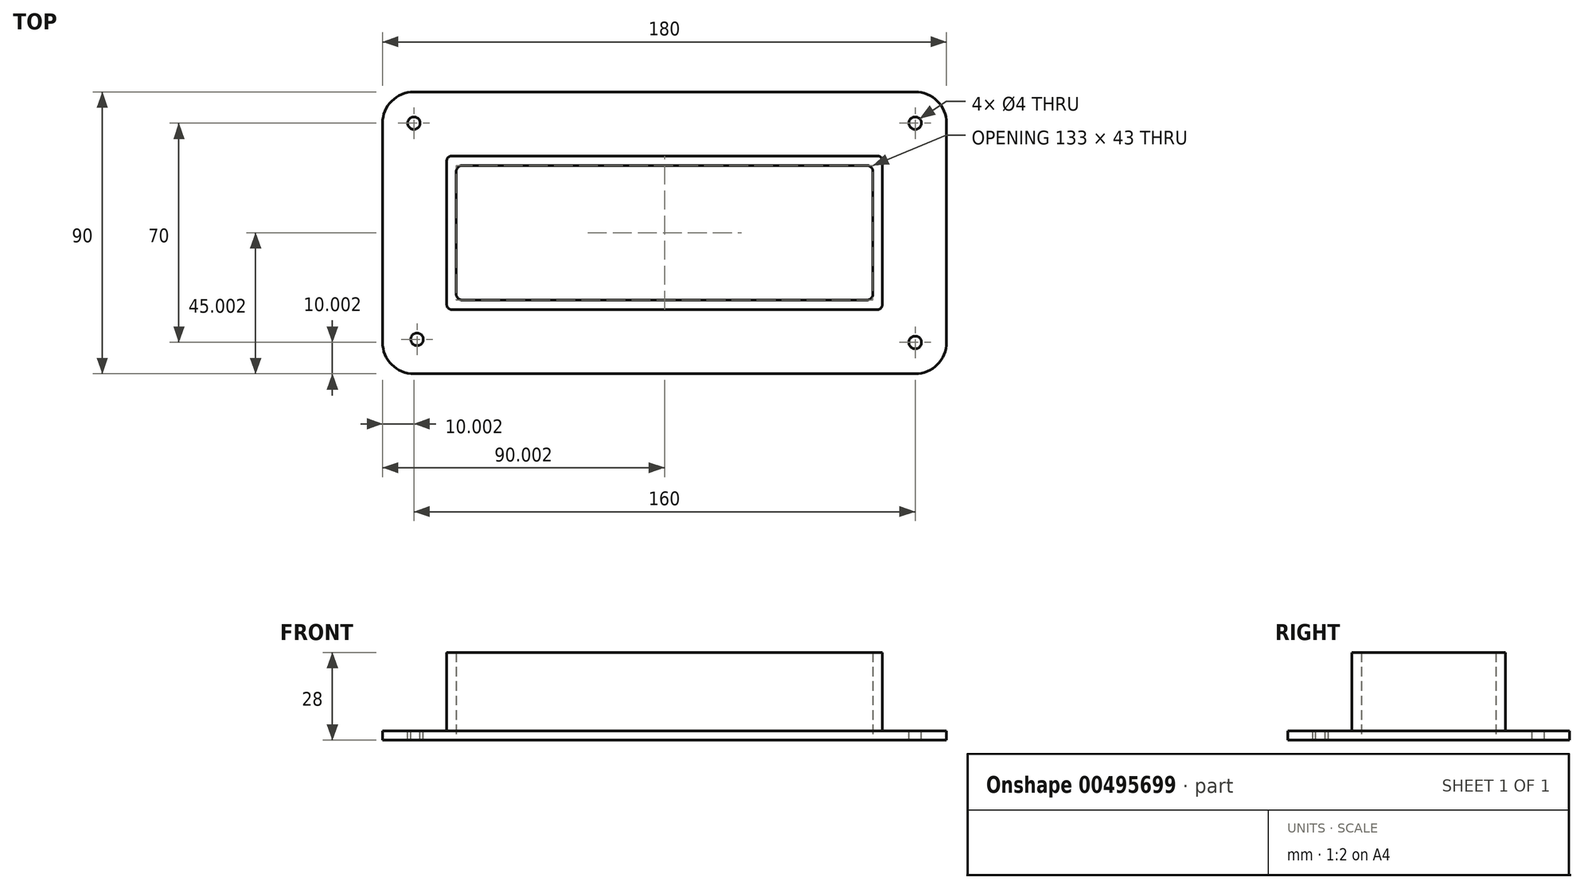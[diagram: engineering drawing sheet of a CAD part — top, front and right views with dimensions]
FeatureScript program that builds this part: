
annotation { "Feature Type Name" : "Feature", "Feature Type Description" : "" }
export const myFeature = defineFeature(function(context is Context, id is Id, definition is map)
    precondition{}
    {
        {
            var Q0;
            Q0=qCreatedBy(makeId("Top.planeOp"),FACE);
            var sketch = newSketch(context, id + "F0", { "sketchPlane" : qUnion([Q0])});
            skLineSegment(sketch, "E0.bottom", {"start": v(-68.03, 24.97) * mm, "end": v(67.97, 24.97) * mm});
            skLineSegment(sketch, "E0.top", {"start": v(-68.03, -25.03) * mm, "end": v(67.97, -25.03) * mm});
            skLineSegment(sketch, "E0.left", {"start": v(-70.03, 22.97) * mm, "end": v(-70.03, -23.03) * mm});
            skLineSegment(sketch, "E0.right", {"start": v(69.97, 22.97) * mm, "end": v(69.97, -23.03) * mm});
            skLineSegment(sketch, "E1.0", {"start": v(-90.03, 34.97) * mm, "end": v(-90.03, -35.03) * mm});
            skLineSegment(sketch, "E1.1", {"start": v(-80.03, 44.97) * mm, "end": v(79.97, 44.97) * mm});
            skLineSegment(sketch, "E1.2", {"start": v(89.97, 34.97) * mm, "end": v(89.97, -35.03) * mm});
            skLineSegment(sketch, "E1.3", {"start": v(-80.03, -45.03) * mm, "end": v(79.97, -45.03) * mm});
            skPoint(sketch, "E2.visualSharp", {"position": v(-90.03, -45.03) * mm});
            skArc(sketch, "E2.filletArc", {"start": v(-90.03, -35.03) * mm, "mid": v(-87.1, -42.1) * mm, "end": v(-80.03, -45.03) * mm});
            skPoint(sketch, "E3.visualSharp", {"position": v(-90.03, 44.97) * mm});
            skArc(sketch, "E3.filletArc", {"start": v(-80.03, 44.97) * mm, "mid": v(-87.1, 42.04) * mm, "end": v(-90.03, 34.97) * mm});
            skPoint(sketch, "E4.visualSharp", {"position": v(89.97, 44.97) * mm});
            skArc(sketch, "E4.filletArc", {"start": v(89.97, 34.97) * mm, "mid": v(87.04, 42.04) * mm, "end": v(79.97, 44.97) * mm});
            skPoint(sketch, "E5.visualSharp", {"position": v(89.97, -45.03) * mm});
            skArc(sketch, "E5.filletArc", {"start": v(79.97, -45.03) * mm, "mid": v(87.04, -42.1) * mm, "end": v(89.97, -35.03) * mm});
            skPoint(sketch, "E6.visualSharp", {"position": v(-70.03, 24.97) * mm});
            skArc(sketch, "E6.filletArc", {"start": v(-68.03, 24.97) * mm, "mid": v(-69.44, 24.39) * mm, "end": v(-70.03, 22.97) * mm});
            skPoint(sketch, "E7.visualSharp", {"position": v(-70.03, -25.03) * mm});
            skArc(sketch, "E7.filletArc", {"start": v(-70.03, -23.03) * mm, "mid": v(-69.44, -24.44) * mm, "end": v(-68.03, -25.03) * mm});
            skPoint(sketch, "E8.visualSharp", {"position": v(69.97, -25.03) * mm});
            skArc(sketch, "E8.filletArc", {"start": v(67.97, -25.03) * mm, "mid": v(69.39, -24.44) * mm, "end": v(69.97, -23.03) * mm});
            skPoint(sketch, "E9.visualSharp", {"position": v(69.97, 24.97) * mm});
            skArc(sketch, "E9.filletArc", {"start": v(69.97, 22.97) * mm, "mid": v(69.39, 24.39) * mm, "end": v(67.97, 24.97) * mm});
            skCircle(sketch, "E10", {"center": v(-80.03, 34.97) * mm, "radius": 2 * mm});
            skCircle(sketch, "E11", {"center": v(-79.03, -34.03) * mm, "radius": 2 * mm});
            skCircle(sketch, "E12", {"center": v(79.97, -35.03) * mm, "radius": 2 * mm});
            skCircle(sketch, "E13", {"center": v(79.97, 34.97) * mm, "radius": 2 * mm});
            skArc(sketch, "E14.0", {"start": v(-68.03, 24.47) * mm, "mid": v(-69.09, 24.03) * mm, "end": v(-69.53, 22.97) * mm});
            skLineSegment(sketch, "E14.1", {"start": v(-68.03, 24.47) * mm, "end": v(67.97, 24.47) * mm});
            skLineSegment(sketch, "E14.2", {"start": v(-69.53, 22.97) * mm, "end": v(-69.53, -23.03) * mm});
            skArc(sketch, "E14.3", {"start": v(69.47, 22.97) * mm, "mid": v(69.03, 24.03) * mm, "end": v(67.97, 24.47) * mm});
            skArc(sketch, "E14.4", {"start": v(-69.53, -23.03) * mm, "mid": v(-69.09, -24.09) * mm, "end": v(-68.03, -24.53) * mm});
            skLineSegment(sketch, "E14.5", {"start": v(-68.03, -24.53) * mm, "end": v(67.97, -24.53) * mm});
            skArc(sketch, "E14.6", {"start": v(67.97, -24.53) * mm, "mid": v(69.03, -24.09) * mm, "end": v(69.47, -23.03) * mm});
            skLineSegment(sketch, "E14.7", {"start": v(69.47, 22.97) * mm, "end": v(69.47, -23.03) * mm});
            skLineSegment(sketch, "E15.0", {"start": v(-66.53, 19.47) * mm, "end": v(-66.53, -19.53) * mm});
            skLineSegment(sketch, "E15.1", {"start": v(-64.53, 21.47) * mm, "end": v(64.47, 21.47) * mm});
            skLineSegment(sketch, "E15.2", {"start": v(66.47, 19.47) * mm, "end": v(66.47, -19.53) * mm});
            skLineSegment(sketch, "E15.3", {"start": v(-64.53, -21.53) * mm, "end": v(64.47, -21.53) * mm});
            skPoint(sketch, "E16.visualSharp", {"position": v(-66.53, 21.47) * mm});
            skArc(sketch, "E16.filletArc", {"start": v(-64.53, 21.47) * mm, "mid": v(-65.94, 20.89) * mm, "end": v(-66.53, 19.47) * mm});
            skPoint(sketch, "E17.visualSharp", {"position": v(-66.53, -21.53) * mm});
            skArc(sketch, "E17.filletArc", {"start": v(-66.53, -19.53) * mm, "mid": v(-65.94, -20.94) * mm, "end": v(-64.53, -21.53) * mm});
            skPoint(sketch, "E18.visualSharp", {"position": v(66.47, -21.53) * mm});
            skArc(sketch, "E18.filletArc", {"start": v(64.47, -21.53) * mm, "mid": v(65.89, -20.94) * mm, "end": v(66.47, -19.53) * mm});
            skPoint(sketch, "E19.visualSharp", {"position": v(66.47, 21.47) * mm});
            skArc(sketch, "E19.filletArc", {"start": v(66.47, 19.47) * mm, "mid": v(65.89, 20.89) * mm, "end": v(64.47, 21.47) * mm});
            skSolve(sketch);
        }
        {
            var Q0;
            Q0=makeQuery(id+"F0.imprint","IMPRINT",FACE,{"disambiguationData":[TD([[makeQuery(id+"F0.imprint","IMPRINT",EDGE,{"derivedFrom":sQuery(id+"F0.wireOp",EDGE,"E14.0")}),1.0]])]});
            extrude(context, id + "F1", {"entities" : qUnion([Q0]), "depth" : 25 * mm});
        }
        {
            var Q0;
            Q0=makeQuery(id+"F0.imprint","IMPRINT",FACE,{"disambiguationData":[TD([[makeQuery(id+"F0.imprint","IMPRINT",EDGE,{"derivedFrom":sQuery(id+"F0.wireOp",EDGE,"E0.bottom")}),1.0]])]});
            var Q1;
            Q1=makeQuery(id+"F0.imprint","IMPRINT",FACE,{"disambiguationData":[TD([[makeQuery(id+"F0.imprint","IMPRINT",EDGE,{"derivedFrom":sQuery(id+"F0.wireOp",EDGE,"E0.bottom")}),-1.0]])]});
            var Q2;
            Q2=makeQuery(id+"F0.imprint","IMPRINT",FACE,{"disambiguationData":[TD([[makeQuery(id+"F0.imprint","IMPRINT",EDGE,{"derivedFrom":sQuery(id+"F0.wireOp",EDGE,"E14.0")}),1.0]])]});
            extrude(context, id + "F2", {"entities" : qUnion([Q0, Q1, Q2]), "operationType" : NewBodyOperationType.ADD, "oppositeDirection" : true, "depth" : 3 * mm});
        }
    });
